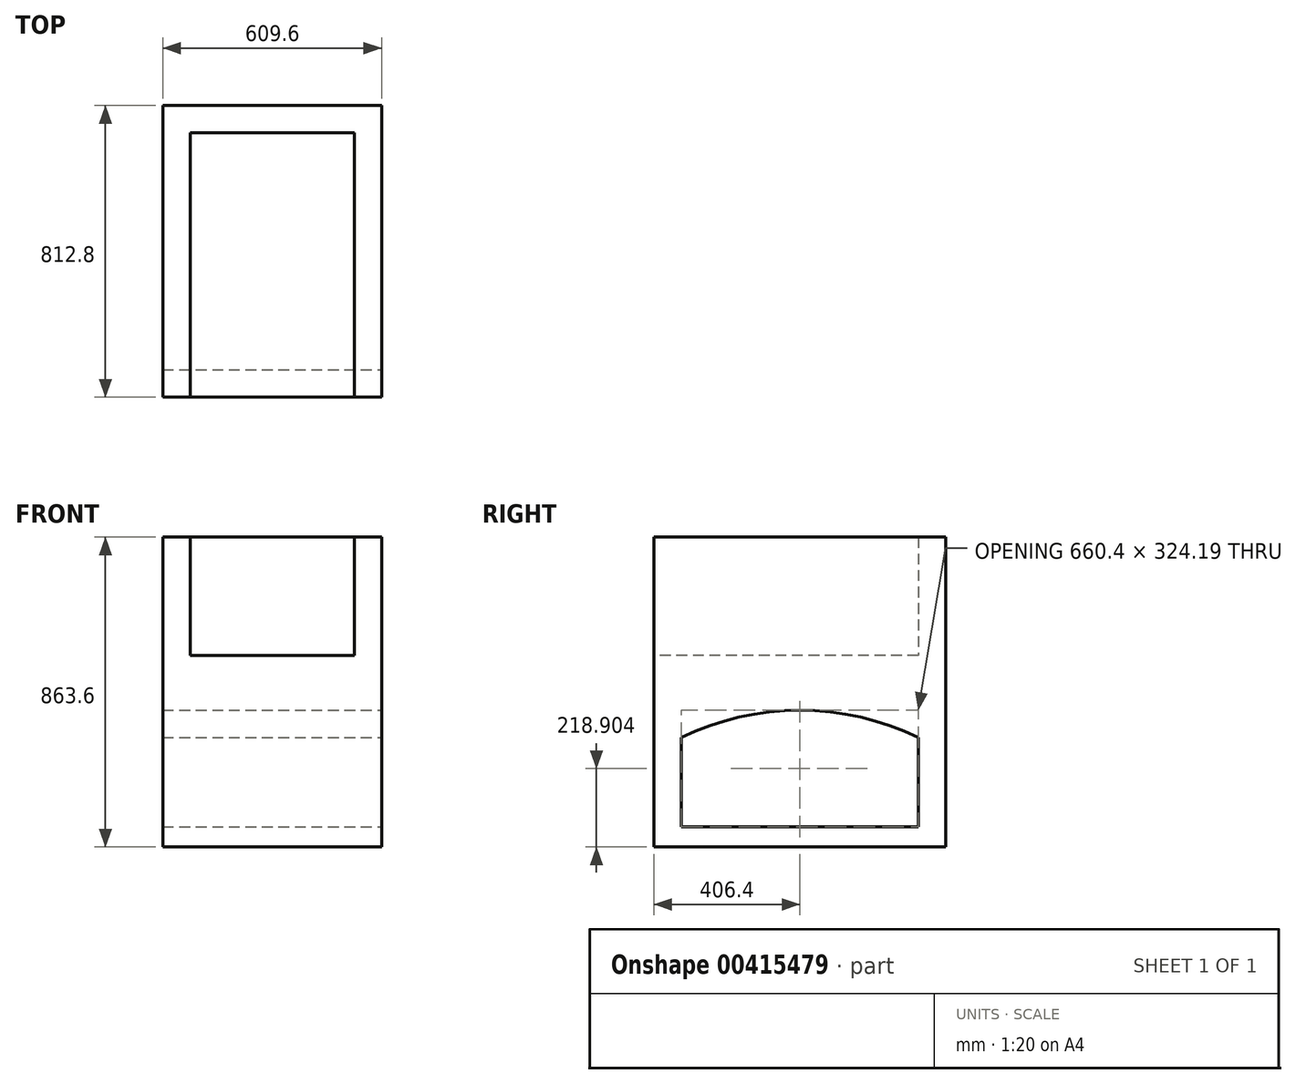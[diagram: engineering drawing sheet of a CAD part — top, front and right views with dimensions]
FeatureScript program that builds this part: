
annotation { "Feature Type Name" : "Feature", "Feature Type Description" : "" }
export const myFeature = defineFeature(function(context is Context, id is Id, definition is map)
    precondition{}
    {
        {
            var Q0;
            Q0=qCreatedBy(makeId("Top.planeOp"),FACE);
            var sketch = newSketch(context, id + "F0", { "sketchPlane" : qUnion([Q0])});
            skLineSegment(sketch, "E0.bottom", {"start": v(304.8, -406.4) * mm, "end": v(-304.8, -406.4) * mm});
            skLineSegment(sketch, "E0.top", {"start": v(304.8, 406.4) * mm, "end": v(-304.8, 406.4) * mm});
            skLineSegment(sketch, "E0.left", {"start": v(304.8, -406.4) * mm, "end": v(304.8, 406.4) * mm});
            skLineSegment(sketch, "E0.right", {"start": v(-304.8, -406.4) * mm, "end": v(-304.8, 406.4) * mm});
            skPoint(sketch, "E0.middle", {"position": v(0, 0) * mm});
            skSolve(sketch);
        }
        {
            var Q0;
            Q0=makeQuery(id+"F0.imprint","IMPRINT",FACE,{"disambiguationData":[TD([[makeQuery(id+"F0.imprint","IMPRINT",EDGE,{"derivedFrom":sQuery(id+"F0.wireOp",EDGE,"E0.bottom")}),-1.0]])]});
            extrude(context, id + "F1", {"entities" : qUnion([Q0]), "depth" : 914.4 * mm});
        }
        {
            var Q0;
            Q0=makeQuery(id+"F1.opExtrude","SWEPT_FACE",FACE,{"disambiguationData":[OSD([sQuery(id+"F0.wireOp",EDGE,"E0.left")])]});
            var sketch = newSketch(context, id + "F2", { "sketchPlane" : qUnion([Q0])});
            skLineSegment(sketch, "E1", {"start": v(-406.4, 457.2) * mm, "end": v(406.4, 457.2) * mm});
            skPoint(sketch, "E2", {"position": v(0, 457.2) * mm});
            skPoint(sketch, "E3", {"position": v(0, 381) * mm});
            skPoint(sketch, "E4", {"position": v(-406.4, 304.8) * mm});
            skPoint(sketch, "E5", {"position": v(406.4, 304.8) * mm});
            skPoint(sketch, "E6", {"position": v(-330.2, 304.8) * mm});
            skPoint(sketch, "E7", {"position": v(330.2, 304.8) * mm});
            skArc(sketch, "E8", {"start": v(330.2, 304.8) * mm, "mid": v(0, 381) * mm, "end": v(-330.2, 304.8) * mm});
            skLineSegment(sketch, "E9", {"start": v(-330.2, 304.8) * mm, "end": v(-330.2, 56.8) * mm});
            skLineSegment(sketch, "E10", {"start": v(-330.2, 56.8) * mm, "end": v(330.2, 56.8) * mm});
            skLineSegment(sketch, "E11", {"start": v(330.2, 56.8) * mm, "end": v(330.2, 304.8) * mm});
            skSolve(sketch);
        }
        {
            var Q0;
            Q0=makeQuery(id+"F1.opExtrude","SWEPT_FACE",FACE,{"disambiguationData":[OSD([sQuery(id+"F0.wireOp",EDGE,"E0.bottom")])]});
            var sketch = newSketch(context, id + "F3", { "sketchPlane" : qUnion([Q0])});
            skLineSegment(sketch, "E12", {"start": v(304.8, 457.2) * mm, "end": v(-304.8, 457.2) * mm});
            skLineSegment(sketch, "E13.bottom", {"start": v(-228.6, 863.6) * mm, "end": v(228.6, 863.6) * mm});
            skLineSegment(sketch, "E13.top", {"start": v(-228.6, 533.4) * mm, "end": v(228.6, 533.4) * mm});
            skLineSegment(sketch, "E13.left", {"start": v(-228.6, 863.6) * mm, "end": v(-228.6, 533.4) * mm});
            skLineSegment(sketch, "E13.right", {"start": v(228.6, 863.6) * mm, "end": v(228.6, 533.4) * mm});
            skSolve(sketch);
        }
        {
            var Q0;
            Q0=makeQuery(id+"F2.imprint","IMPRINT",FACE,{"disambiguationData":[TD([[makeQuery(id+"F2.imprint","IMPRINT",EDGE,{"derivedFrom":sQuery(id+"F2.wireOp",EDGE,"E8")}),1.0]])]});
            extrude(context, id + "F4", {"entities" : qUnion([Q0]), "operationType" : NewBodyOperationType.REMOVE, "endBound" : BoundingType.THROUGH_ALL, "oppositeDirection" : true, "depth" : 25.4 * mm});
        }
        {
            var Q0;
            Q0=makeQuery(id+"F3.imprint","IMPRINT",FACE,{"disambiguationData":[TD([[makeQuery(id+"F3.imprint","IMPRINT",EDGE,{"derivedFrom":sQuery(id+"F3.wireOp",EDGE,"E13.bottom")}),-1.0]])]});
            extrude(context, id + "F5", {"entities" : qUnion([Q0]), "operationType" : NewBodyOperationType.REMOVE, "oppositeDirection" : true, "depth" : 736.6 * mm});
        }
        {
            var Q0;
            Q0=makeQuery(id+"F1.opExtrude","CAP_FACE",FACE,{"disambiguationData":[OSD([sQuery(id+"F0.wireOp",EDGE,"E0.bottom"),sQuery(id+"F0.wireOp",EDGE,"E0.top"),sQuery(id+"F0.wireOp",EDGE,"E0.left"),sQuery(id+"F0.wireOp",EDGE,"E0.right")])],"isStart":false});
            extrude(context, id + "F6", {"entities" : qUnion([Q0]), "operationType" : NewBodyOperationType.REMOVE, "oppositeDirection" : true, "depth" : 50.8 * mm});
        }
    });
